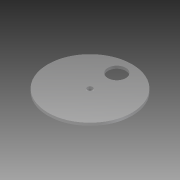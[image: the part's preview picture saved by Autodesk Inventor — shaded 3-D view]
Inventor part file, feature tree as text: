
AUTODESK INVENTOR PART (.ipt)
format: ipt  version: 2012 (Build 160160000, 160)  size: 76,800 bytes
history: native  units: mm
features: extrude x1, sketch x1
ambient origin geometry x8: Origin, YZ Plane, XZ Plane, XY Plane, X Axis, Y Axis, Z Axis, Center Point
feature tree (2):
  extrude  "Extrusion2"  Depth=5.9mm
  sketch  "Sketch1"  dims[d0=94.0mm d1=5.9mm d4=20.0mm d5=30.0mm d6=3.0mm d7=0.0mm]
